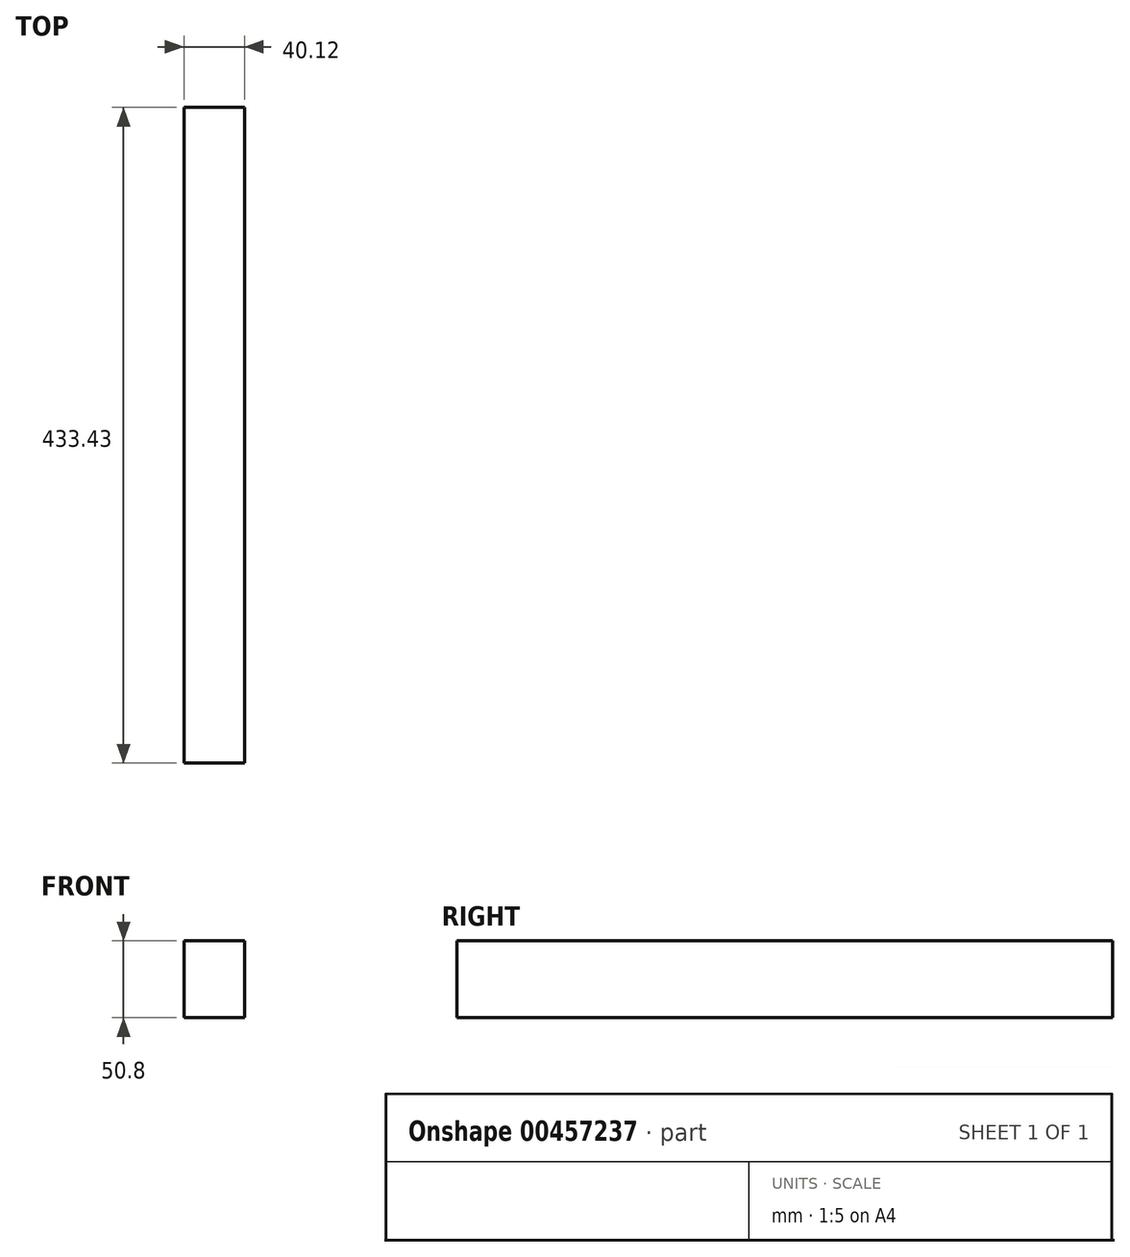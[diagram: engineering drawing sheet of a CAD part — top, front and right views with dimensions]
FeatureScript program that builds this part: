
annotation { "Feature Type Name" : "Feature", "Feature Type Description" : "" }
export const myFeature = defineFeature(function(context is Context, id is Id, definition is map)
    precondition{}
    {
        {
            var Q0;
            Q0=qCreatedBy(makeId("Top.planeOp"),FACE);
            var sketch = newSketch(context, id + "F0", { "sketchPlane" : qUnion([Q0])});
            skLineSegment(sketch, "E0.bottom", {"start": v(0, 74.5) * mm, "end": v(-40.12, 74.5) * mm});
            skLineSegment(sketch, "E0.top", {"start": v(0, -358.93) * mm, "end": v(-40.12, -358.93) * mm});
            skLineSegment(sketch, "E0.left", {"start": v(0, 74.5) * mm, "end": v(0, -358.93) * mm});
            skLineSegment(sketch, "E0.right", {"start": v(-40.12, 74.5) * mm, "end": v(-40.12, -358.93) * mm});
            skPoint(sketch, "E0.middle", {"position": v(-20.06, -142.21) * mm});
            skSolve(sketch);
        }
        {
            var Q0;
            Q0 = qSketchRegion(id + "F0", true);
            extrude(context, id + "F1", {"entities" : qUnion([Q0]), "depth" : 25.4 * mm});
        }
        {
            var Q0;
            Q0=makeQuery(id+"F1.opExtrude","CAP_FACE",FACE,{"disambiguationData":[OSD([sQuery(id+"F0.wireOp",EDGE,"E0.bottom"),sQuery(id+"F0.wireOp",EDGE,"E0.top"),sQuery(id+"F0.wireOp",EDGE,"E0.left"),sQuery(id+"F0.wireOp",EDGE,"E0.right")])],"isStart":false});
            var sketch = newSketch(context, id + "F2", { "sketchPlane" : qUnion([Q0])});
            skCircle(sketch, "E1", {"center": v(0, -292.46) * mm, "radius": 36.4 * mm, "construction": true});
            skSolve(sketch);
        }
        {
            var Q0;
            Q0=makeQuery(id+"F2.imprint","IMPRINT",FACE,{"disambiguationData":[TD([[makeQuery(id+"F2.imprint","IMPRINT",EDGE,{"derivedFrom":makeQuery(id+"F1.opExtrude","CAP_EDGE",EDGE,{"disambiguationData":[OSD([sQuery(id+"F0.wireOp",EDGE,"E0.bottom")])],"isStart":false})}),1.0]])]});
            extrude(context, id + "F3", {"entities" : qUnion([Q0]), "operationType" : NewBodyOperationType.ADD, "depth" : 25.4 * mm});
        }
        {
            var Q0;
            Q0=makeQuery(id+"F1.opExtrude","CAP_FACE",FACE,{"disambiguationData":[OSD([sQuery(id+"F0.wireOp",EDGE,"E0.bottom"),sQuery(id+"F0.wireOp",EDGE,"E0.top"),sQuery(id+"F0.wireOp",EDGE,"E0.left"),sQuery(id+"F0.wireOp",EDGE,"E0.right")])],"isStart":true});
            var sketch = newSketch(context, id + "F4", { "sketchPlane" : qUnion([Q0])});
            skLineSegment(sketch, "E2.bottom", {"start": v(0, 328.7) * mm, "end": v(-23.11, 328.7) * mm});
            skLineSegment(sketch, "E2.top", {"start": v(0, 296.03) * mm, "end": v(-23.11, 296.03) * mm});
            skLineSegment(sketch, "E2.left", {"start": v(0, 328.7) * mm, "end": v(0, 296.03) * mm});
            skLineSegment(sketch, "E2.right", {"start": v(-23.11, 328.7) * mm, "end": v(-23.11, 296.03) * mm});
            skSolve(sketch);
        }
        {
            var Q0;
            Q0=sQuery(id+"F4.wireOp",EDGE,"E2.bottom");
            extrude(context, id + "F5", {"bodyType" : ToolBodyType.SURFACE, "surfaceEntities" : qUnion([Q0]), "oppositeDirection" : true, "depth" : 198.44 * mm});
        }
    });
